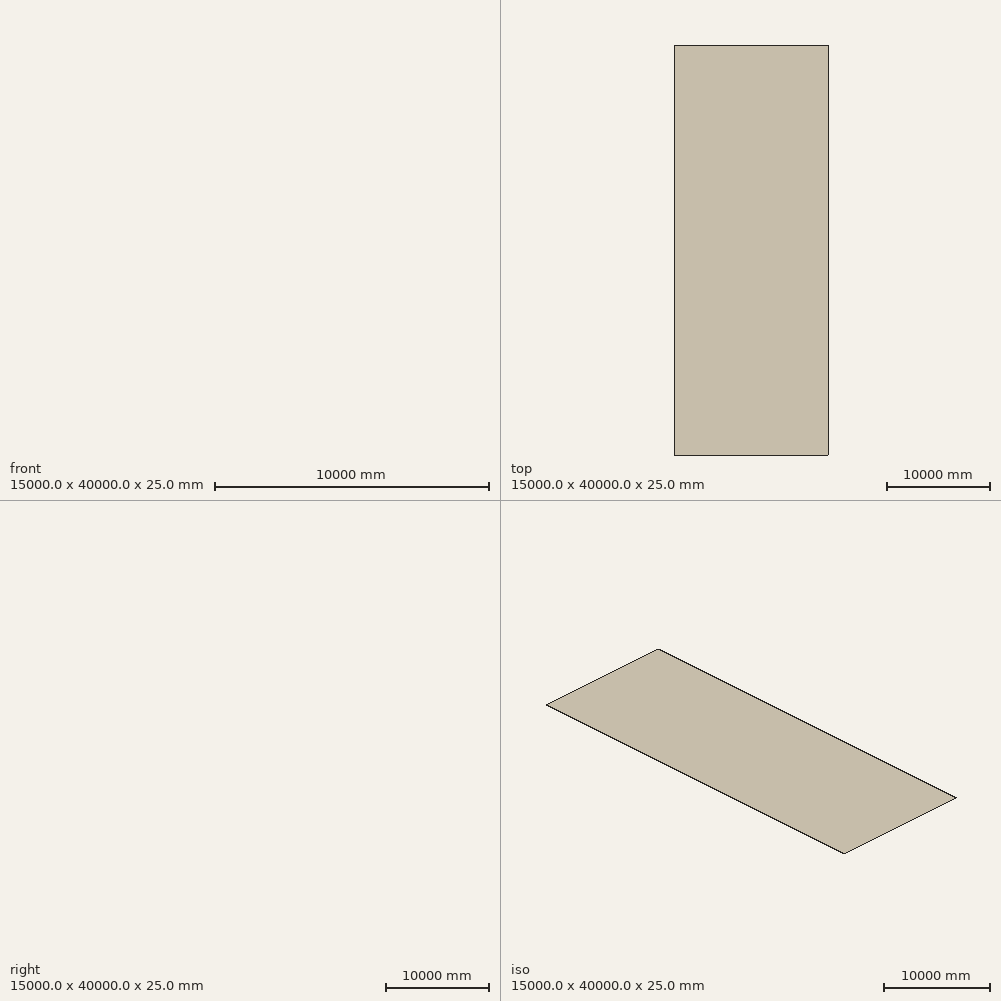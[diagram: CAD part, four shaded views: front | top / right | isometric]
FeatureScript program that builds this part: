
annotation { "Feature Type Name" : "Feature", "Feature Type Description" : "" }
export const myFeature = defineFeature(function(context is Context, id is Id, definition is map)
    precondition{}
    {
        {
            var Q0;
            Q0=qCreatedBy(makeId("Top.planeOp"),FACE);
            var sketch = newSketch(context, id + "F0", { "sketchPlane" : qUnion([Q0])});
            skLineSegment(sketch, "E0.bottom", {"start": v(-7500, 20000) * mm, "end": v(7500, 20000) * mm});
            skLineSegment(sketch, "E0.top", {"start": v(-7500, -20000) * mm, "end": v(7500, -20000) * mm});
            skLineSegment(sketch, "E0.left", {"start": v(-7500, 20000) * mm, "end": v(-7500, -20000) * mm});
            skLineSegment(sketch, "E0.right", {"start": v(7500, 20000) * mm, "end": v(7500, -20000) * mm});
            skPoint(sketch, "E0.middle", {"position": v(0, 0) * mm});
            skSolve(sketch);
        }
        {
            var Q0;
            Q0=makeQuery(id+"F0.imprint","IMPRINT",FACE,{"disambiguationData":[TD([[makeQuery(id+"F0.imprint","IMPRINT",EDGE,{"derivedFrom":sQuery(id+"F0.wireOp",EDGE,"E0.bottom")}),-1.0]])]});
            extrude(context, id + "F1", {"entities" : qUnion([Q0]), "depth" : 25 * mm, "offsetDistance" : 25 * mm});
        }
    });
